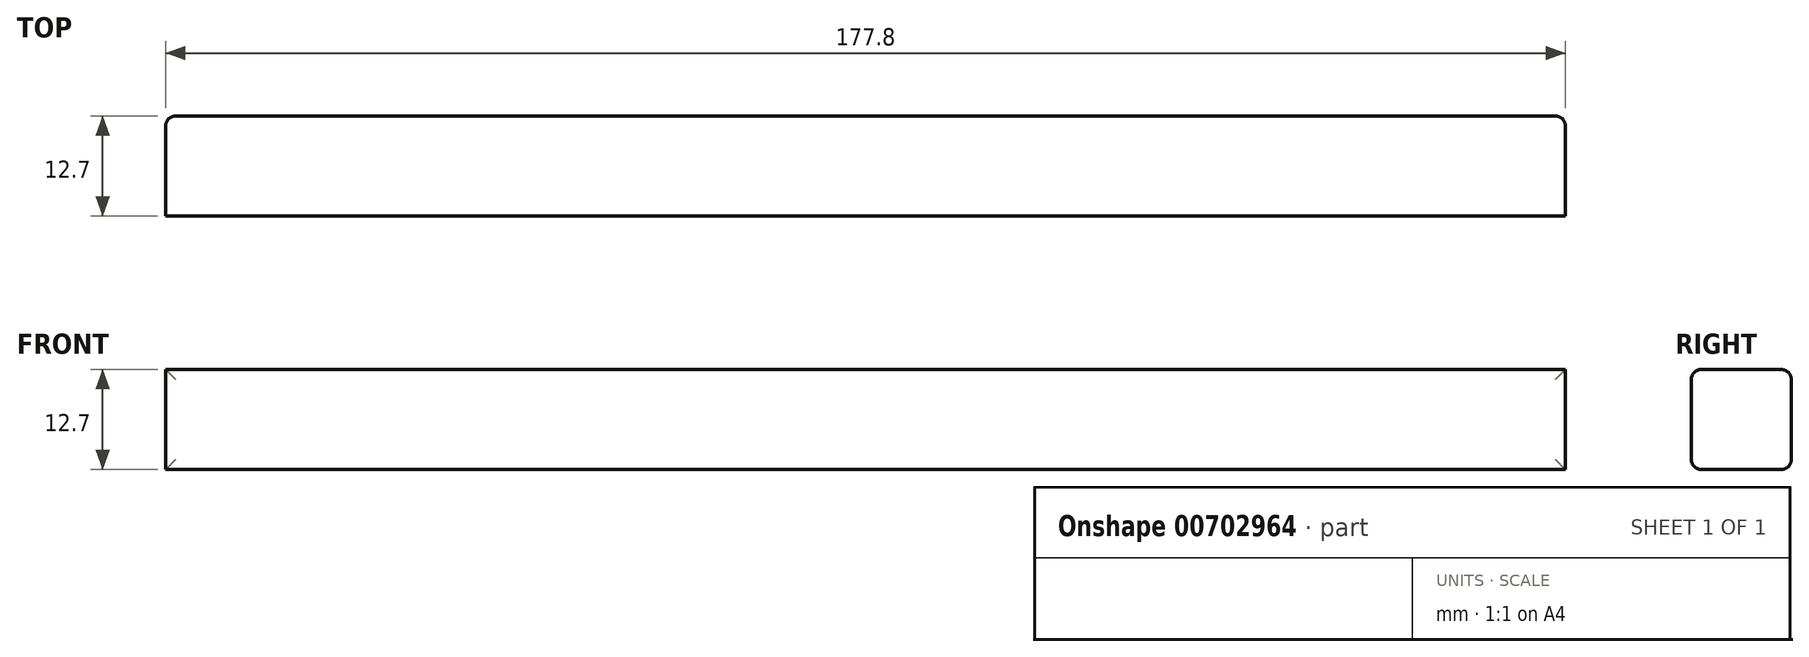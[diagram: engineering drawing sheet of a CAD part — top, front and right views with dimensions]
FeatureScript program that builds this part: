
annotation { "Feature Type Name" : "Feature", "Feature Type Description" : "" }
export const myFeature = defineFeature(function(context is Context, id is Id, definition is map)
    precondition{}
    {
        {
            var Q0;
            Q0=qCreatedBy(makeId("Top.planeOp"),FACE);
            var sketch = newSketch(context, id + "F0", { "sketchPlane" : qUnion([Q0])});
            skLineSegment(sketch, "E0.bottom", {"start": v(88.9, -6.35) * mm, "end": v(-88.9, -6.35) * mm});
            skLineSegment(sketch, "E0.top", {"start": v(88.9, 6.35) * mm, "end": v(-88.9, 6.35) * mm});
            skLineSegment(sketch, "E0.left", {"start": v(88.9, -6.35) * mm, "end": v(88.9, 6.35) * mm});
            skLineSegment(sketch, "E0.right", {"start": v(-88.9, -6.35) * mm, "end": v(-88.9, 6.35) * mm});
            skPoint(sketch, "E0.middle", {"position": v(0, 0) * mm});
            skSolve(sketch);
        }
        {
            var Q0;
            Q0=makeQuery(id+"F0.imprint","IMPRINT",FACE,{"disambiguationData":[TD([[makeQuery(id+"F0.imprint","IMPRINT",EDGE,{"derivedFrom":sQuery(id+"F0.wireOp",EDGE,"E0.bottom")}),-1.0]])]});
            extrude(context, id + "F1", {"entities" : qUnion([Q0]), "depth" : 12.7 * mm, "offsetDistance" : 25.4 * mm});
        }
        {
            var Q0;
            Q0=makeQuery(id+"F1.opExtrude","CAP_EDGE",EDGE,{"disambiguationData":[OSD([sQuery(id+"F0.wireOp",EDGE,"E0.top")])],"isStart":false});
            var Q1;
            Q1=makeQuery(id+"F1.opExtrude","CAP_EDGE",EDGE,{"disambiguationData":[OSD([sQuery(id+"F0.wireOp",EDGE,"E0.bottom")])],"isStart":false});
            var Q2;
            Q2=makeQuery(id+"F1.opExtrude","SWEPT_FACE",FACE,{"disambiguationData":[OSD([sQuery(id+"F0.wireOp",EDGE,"E0.top")])]});
            var Q3;
            Q3=makeQuery(id+"F1.opExtrude","CAP_EDGE",EDGE,{"disambiguationData":[OSD([sQuery(id+"F0.wireOp",EDGE,"E0.bottom")])],"isStart":true});
            fillet(context, id + "F2", {"entities" : qUnion([Q0, Q1, Q2, Q3]), "radius" : 1.27 * mm, "tangentPropagation" : true, "allowEdgeOverflow" : false});
        }
    });
